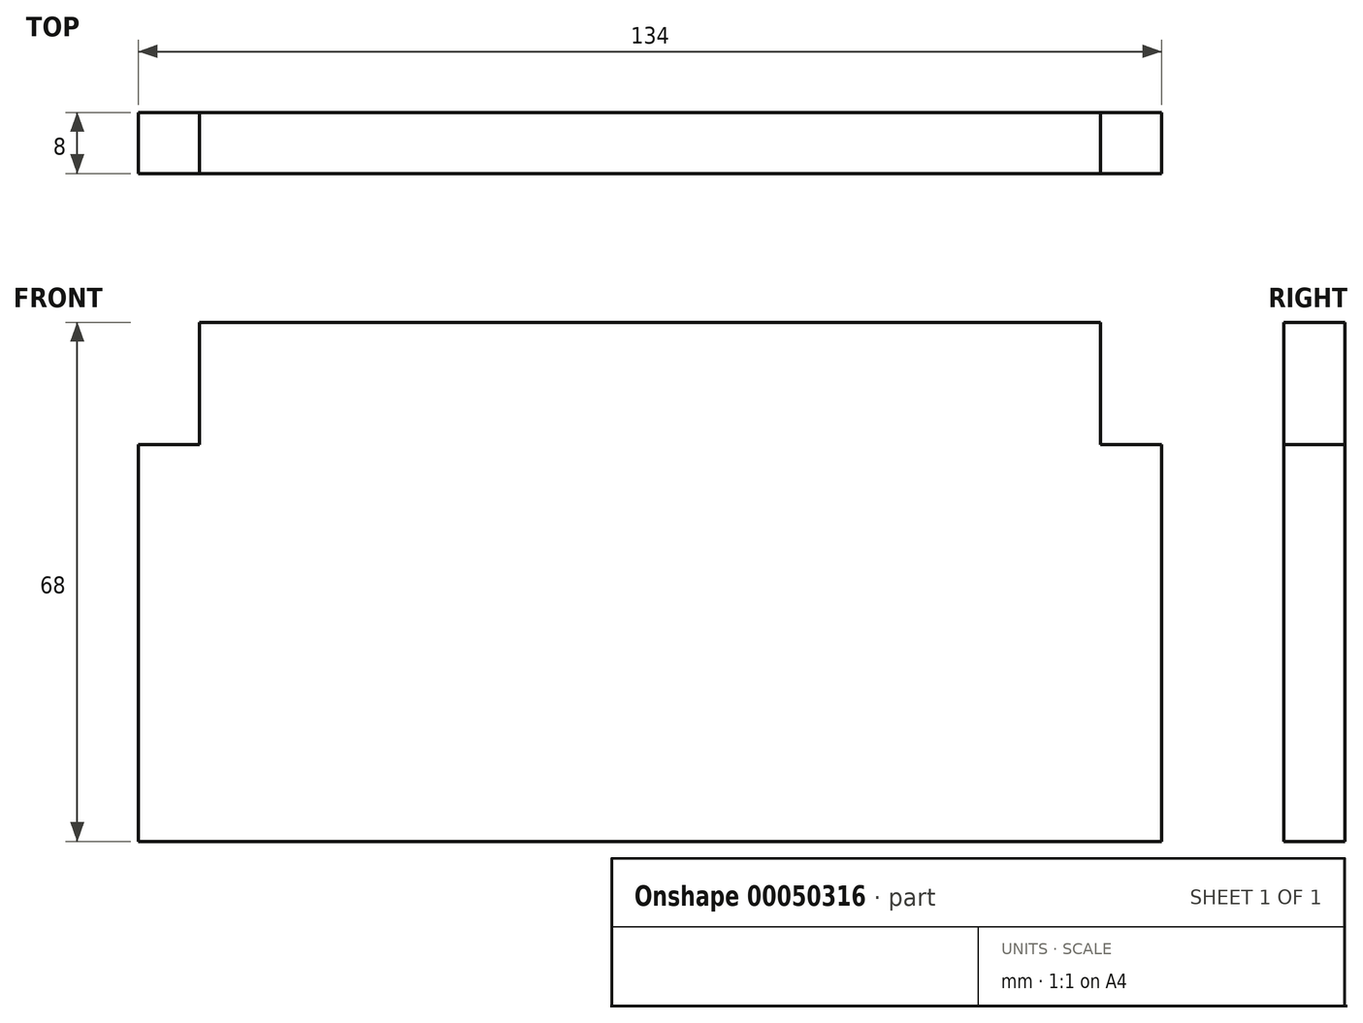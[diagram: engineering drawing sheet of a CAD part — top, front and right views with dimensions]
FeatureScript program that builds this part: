
annotation { "Feature Type Name" : "Feature", "Feature Type Description" : "" }
export const myFeature = defineFeature(function(context is Context, id is Id, definition is map)
    precondition{}
    {
        {
            var Q0;
            Q0=qCreatedBy(makeId("Front.planeOp"),FACE);
            var sketch = newSketch(context, id + "F0", { "sketchPlane" : qUnion([Q0])});
            skLineSegment(sketch, "E0.bottom", {"start": v(0, 0) * mm, "end": v(-118, 0) * mm});
            skLineSegment(sketch, "E0.top", {"start": v(8, -68) * mm, "end": v(-126, -68) * mm});
            skLineSegment(sketch, "E0.right", {"start": v(-126, -16) * mm, "end": v(-126, -68) * mm});
            skLineSegment(sketch, "E1.top", {"start": v(-118, -16) * mm, "end": v(-126, -16) * mm});
            skLineSegment(sketch, "E1.left", {"start": v(-118, 0) * mm, "end": v(-118, -16) * mm});
            skLineSegment(sketch, "E2.top", {"start": v(8, -16) * mm, "end": v(0, -16) * mm});
            skLineSegment(sketch, "E2.right", {"start": v(0, 0) * mm, "end": v(0, -16) * mm});
            skLineSegment(sketch, "E3", {"start": v(8, -68) * mm, "end": v(8, -16) * mm});
            skSolve(sketch);
        }
        {
            var Q0;
            Q0 = qSketchRegion(id + "F0", true);
            extrude(context, id + "F1", {"entities" : qUnion([Q0]), "depth" : 8 * mm});
        }
    });
